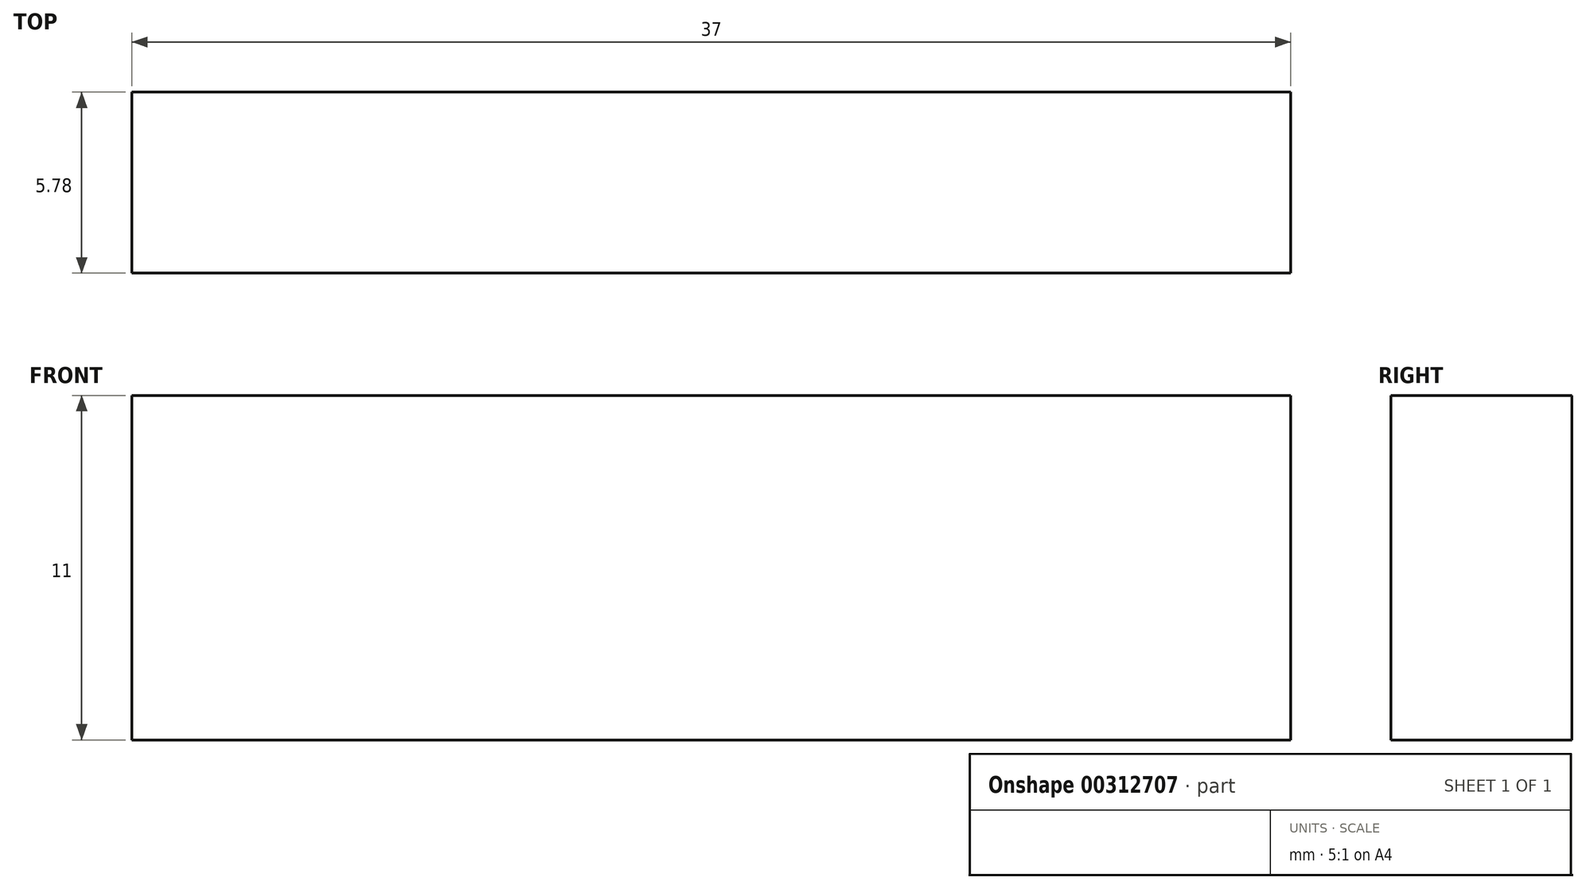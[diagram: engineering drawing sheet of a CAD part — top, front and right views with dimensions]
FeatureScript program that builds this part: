
annotation { "Feature Type Name" : "Feature", "Feature Type Description" : "" }
export const myFeature = defineFeature(function(context is Context, id is Id, definition is map)
    precondition{}
    {
        {
            var Q0;
            Q0=qCreatedBy(makeId("Top.planeOp"),FACE);
            var sketch = newSketch(context, id + "F0", { "sketchPlane" : qUnion([Q0])});
            skLineSegment(sketch, "E0.bottom", {"start": v(0, 0) * mm, "end": v(37, 0) * mm});
            skLineSegment(sketch, "E0.top", {"start": v(0, -11) * mm, "end": v(37, -11) * mm});
            skLineSegment(sketch, "E0.left", {"start": v(0, 0) * mm, "end": v(0, -11) * mm});
            skLineSegment(sketch, "E0.right", {"start": v(37, 0) * mm, "end": v(37, -11) * mm});
            skLineSegment(sketch, "E1.bottom", {"start": v(16, -11) * mm, "end": v(0, -11) * mm});
            skLineSegment(sketch, "E1.top", {"start": v(16, -5.78) * mm, "end": v(0, -5.78) * mm});
            skLineSegment(sketch, "E1.left", {"start": v(16, -11) * mm, "end": v(16, -5.78) * mm});
            skLineSegment(sketch, "E1.right", {"start": v(0, -11) * mm, "end": v(0, -5.78) * mm});
            skLineSegment(sketch, "E2", {"start": v(16, -5.78) * mm, "end": v(37, -5.78) * mm});
            skSolve(sketch);
        }
        {
            var Q0;
            Q0=makeQuery(id+"F0.imprint","IMPRINT",FACE,{"disambiguationData":[TD([[makeQuery(id+"F0.imprint","IMPRINT",EDGE,{"derivedFrom":sQuery(id+"F0.wireOp",EDGE,"E0.bottom")}),-1.0]])]});
            var Q1;
            Q1=makeQuery(id+"F0.imprint","IMPRINT",FACE,{"disambiguationData":[TD([[makeQuery(id+"F0.imprint","IMPRINT",EDGE,{"derivedFrom":sQuery(id+"F0.wireOp",EDGE,"E1.bottom")}),-1.0]])]});
            extrude(context, id + "F1", {"entities" : qUnion([Q0, Q1]), "depth" : 11 * mm});
        }
    });
